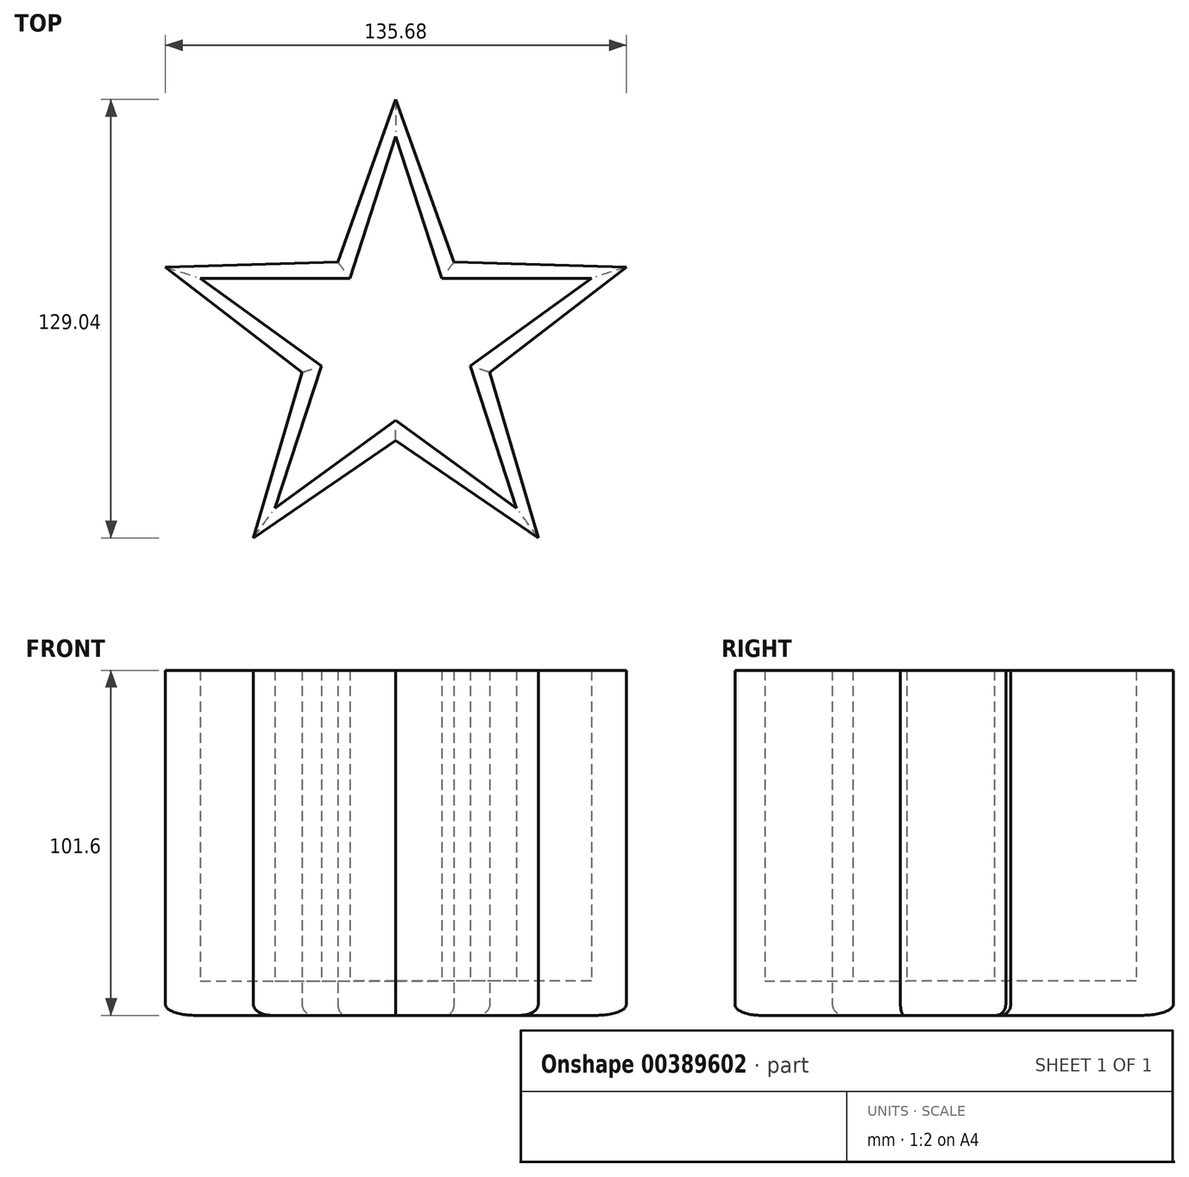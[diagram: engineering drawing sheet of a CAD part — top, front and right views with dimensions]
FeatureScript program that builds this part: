
annotation { "Feature Type Name" : "Feature", "Feature Type Description" : "" }
export const myFeature = defineFeature(function(context is Context, id is Id, definition is map)
    precondition{}
    {
        {
            var Q0;
            Q0=qCreatedBy(makeId("Top.planeOp"),FACE);
            var sketch = newSketch(context, id + "F0", { "sketchPlane" : qUnion([Q0])});
            skLineSegment(sketch, "E0.MirrorCS", {"start": v(17.06, 23.48) * mm, "end": v(0, 71.33) * mm});
            skLineSegment(sketch, "E1.1.0", {"start": v(-27.6, -8.97) * mm, "end": v(-67.84, 22.04) * mm});
            skLineSegment(sketch, "E1.1.1", {"start": v(-17.06, 23.48) * mm, "end": v(-67.84, 22.04) * mm});
            skLineSegment(sketch, "E1.2.0", {"start": v(0, -29.03) * mm, "end": v(-41.93, -57.7) * mm});
            skLineSegment(sketch, "E1.3.0", {"start": v(27.6, -8.97) * mm, "end": v(41.93, -57.7) * mm});
            skLineSegment(sketch, "E1.4.0", {"start": v(17.06, 23.48) * mm, "end": v(67.84, 22.04) * mm});
            skPoint(sketch, "E1.center", {"position": v(0, 0) * mm});
            skLineSegment(sketch, "E2.trimOffspring", {"start": v(-17.06, 23.48) * mm, "end": v(0, 71.33) * mm});
            skLineSegment(sketch, "E3.trimOffspring", {"start": v(-27.6, -8.97) * mm, "end": v(-41.93, -57.7) * mm});
            skLineSegment(sketch, "E4.trimOffspring", {"start": v(27.6, -8.97) * mm, "end": v(67.84, 22.04) * mm});
            skLineSegment(sketch, "E5.trimOffspring", {"start": v(0, -29.03) * mm, "end": v(41.93, -57.7) * mm});
            skLineSegment(sketch, "E6.MirrorCS", {"start": v(0, 60.5) * mm, "end": v(-14.08, 17) * mm});
            skLineSegment(sketch, "E7.MirrorCS", {"start": v(0, 60.5) * mm, "end": v(14.08, 17) * mm});
            skLineSegment(sketch, "E8.1.0", {"start": v(-57.54, 18.7) * mm, "end": v(-20.52, -8.14) * mm});
            skLineSegment(sketch, "E8.1.1", {"start": v(-57.54, 18.7) * mm, "end": v(-11.82, 18.65) * mm});
            skLineSegment(sketch, "E8.2.0", {"start": v(-35.56, -48.95) * mm, "end": v(1.4, -22.03) * mm});
            skLineSegment(sketch, "E8.2.1", {"start": v(-35.56, -48.95) * mm, "end": v(-21.39, -5.48) * mm});
            skLineSegment(sketch, "E8.3.0", {"start": v(35.56, -48.95) * mm, "end": v(21.39, -5.48) * mm});
            skLineSegment(sketch, "E8.3.1", {"start": v(35.56, -48.95) * mm, "end": v(-1.4, -22.03) * mm});
            skLineSegment(sketch, "E8.4.0", {"start": v(57.54, 18.7) * mm, "end": v(11.82, 18.65) * mm});
            skLineSegment(sketch, "E8.4.1", {"start": v(57.54, 18.7) * mm, "end": v(20.52, -8.14) * mm});
            skLineSegment(sketch, "E9", {"start": v(0, 23.47) * mm, "end": v(0, 71.33) * mm});
            skSolve(sketch);
        }
        {
            var Q0;
            Q0 = qSketchRegion(id + "F0", true);
            extrude(context, id + "F1", {"entities" : qUnion([Q0]), "endBound" : BoundingType.SYMMETRIC, "depth" : 101.6 * mm});
        }
        {
            var Q0;
            Q0=makeQuery(id+"F1.opExtrude","CAP_FACE",FACE,{"disambiguationData":[OSD([sQuery(id+"F0.wireOp",EDGE,"E0.MirrorCS"),sQuery(id+"F0.wireOp",EDGE,"E1.1.0"),sQuery(id+"F0.wireOp",EDGE,"E1.1.1"),sQuery(id+"F0.wireOp",EDGE,"E1.2.0"),sQuery(id+"F0.wireOp",EDGE,"E1.3.0"),sQuery(id+"F0.wireOp",EDGE,"E1.4.0"),sQuery(id+"F0.wireOp",EDGE,"E2.trimOffspring"),sQuery(id+"F0.wireOp",EDGE,"E3.trimOffspring"),sQuery(id+"F0.wireOp",EDGE,"E4.trimOffspring"),sQuery(id+"F0.wireOp",EDGE,"E5.trimOffspring"),sQuery(id+"F0.wireOp",EDGE,"E6.MirrorCS"),sQuery(id+"F0.wireOp",EDGE,"E7.MirrorCS"),sQuery(id+"F0.wireOp",EDGE,"E8.1.0"),sQuery(id+"F0.wireOp",EDGE,"E8.1.1"),sQuery(id+"F0.wireOp",EDGE,"E8.2.0"),sQuery(id+"F0.wireOp",EDGE,"E8.2.1"),sQuery(id+"F0.wireOp",EDGE,"E8.3.0"),sQuery(id+"F0.wireOp",EDGE,"E8.3.1"),sQuery(id+"F0.wireOp",EDGE,"E8.4.0"),sQuery(id+"F0.wireOp",EDGE,"E8.4.1")])],"isStart":true});
            var sketch = newSketch(context, id + "F2", { "sketchPlane" : qUnion([Q0])});
            skLineSegment(sketch, "E10", {"start": v(-35.56, 48.95) * mm, "end": v(-21.92, 7.12) * mm});
            skLineSegment(sketch, "E11", {"start": v(-21.92, 7.12) * mm, "end": v(-57.54, -18.7) * mm});
            skLineSegment(sketch, "E12", {"start": v(-57.54, -18.7) * mm, "end": v(-13.55, -18.65) * mm});
            skLineSegment(sketch, "E13", {"start": v(-13.55, -18.65) * mm, "end": v(0, -60.5) * mm});
            skLineSegment(sketch, "E14", {"start": v(0, -60.5) * mm, "end": v(13.55, -18.65) * mm});
            skLineSegment(sketch, "E15", {"start": v(13.55, -18.65) * mm, "end": v(57.54, -18.7) * mm});
            skLineSegment(sketch, "E16", {"start": v(57.54, -18.7) * mm, "end": v(21.92, 7.12) * mm});
            skLineSegment(sketch, "E17", {"start": v(21.92, 7.12) * mm, "end": v(35.56, 48.95) * mm});
            skLineSegment(sketch, "E18", {"start": v(35.56, 48.95) * mm, "end": v(0, 23.05) * mm});
            skLineSegment(sketch, "E19", {"start": v(0, 23.05) * mm, "end": v(-35.56, 48.95) * mm});
            skSolve(sketch);
        }
        {
            var Q0;
            Q0 = qSketchRegion(id + "F2", true);
            extrude(context, id + "F3", {"entities" : qUnion([Q0]), "operationType" : NewBodyOperationType.ADD, "oppositeDirection" : true, "depth" : 10.16 * mm});
        }
        {
            var Q0;
            Q0=makeQuery(id+"F3.boolean.opBoolean","MERGE",FACE,{"derivedFrom":[makeQuery(id+"F1.opExtrude","CAP_FACE",FACE,{"disambiguationData":[OSD([sQuery(id+"F0.wireOp",EDGE,"E0.MirrorCS"),sQuery(id+"F0.wireOp",EDGE,"E1.1.0"),sQuery(id+"F0.wireOp",EDGE,"E1.1.1"),sQuery(id+"F0.wireOp",EDGE,"E1.2.0"),sQuery(id+"F0.wireOp",EDGE,"E1.3.0"),sQuery(id+"F0.wireOp",EDGE,"E1.4.0"),sQuery(id+"F0.wireOp",EDGE,"E2.trimOffspring"),sQuery(id+"F0.wireOp",EDGE,"E3.trimOffspring"),sQuery(id+"F0.wireOp",EDGE,"E4.trimOffspring"),sQuery(id+"F0.wireOp",EDGE,"E5.trimOffspring"),sQuery(id+"F0.wireOp",EDGE,"E6.MirrorCS"),sQuery(id+"F0.wireOp",EDGE,"E7.MirrorCS"),sQuery(id+"F0.wireOp",EDGE,"E8.1.0"),sQuery(id+"F0.wireOp",EDGE,"E8.1.1"),sQuery(id+"F0.wireOp",EDGE,"E8.2.0"),sQuery(id+"F0.wireOp",EDGE,"E8.2.1"),sQuery(id+"F0.wireOp",EDGE,"E8.3.0"),sQuery(id+"F0.wireOp",EDGE,"E8.3.1"),sQuery(id+"F0.wireOp",EDGE,"E8.4.0"),sQuery(id+"F0.wireOp",EDGE,"E8.4.1")])],"isStart":true}),makeQuery(id+"F3.opExtrude","CAP_FACE",FACE,{"disambiguationData":[OSD([sQuery(id+"F2.wireOp",EDGE,"E10"),sQuery(id+"F2.wireOp",EDGE,"E11"),sQuery(id+"F2.wireOp",EDGE,"E12"),sQuery(id+"F2.wireOp",EDGE,"E13"),sQuery(id+"F2.wireOp",EDGE,"E14"),sQuery(id+"F2.wireOp",EDGE,"E15"),sQuery(id+"F2.wireOp",EDGE,"E16"),sQuery(id+"F2.wireOp",EDGE,"E17"),sQuery(id+"F2.wireOp",EDGE,"E18"),sQuery(id+"F2.wireOp",EDGE,"E19")])],"isStart":true})]});
            fillet(context, id + "F4", {"entities" : qUnion([Q0]), "radius" : 3.17 * mm, "tangentPropagation" : true, "allowEdgeOverflow" : false});
        }
    });
